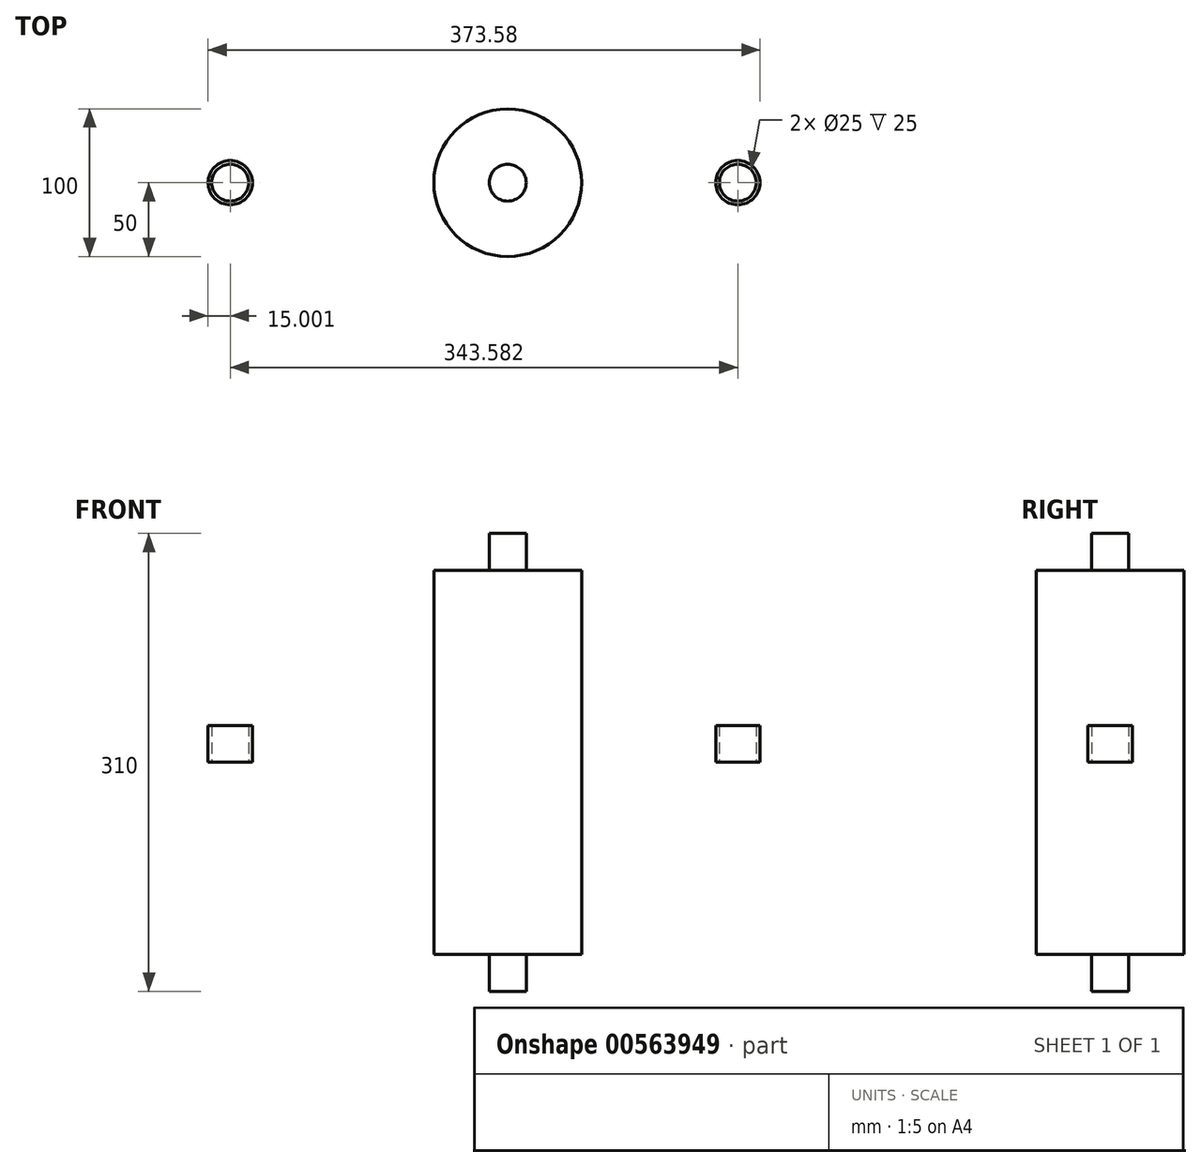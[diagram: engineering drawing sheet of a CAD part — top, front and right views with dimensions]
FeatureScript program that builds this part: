
annotation { "Feature Type Name" : "Feature", "Feature Type Description" : "" }
export const myFeature = defineFeature(function(context is Context, id is Id, definition is map)
    precondition{}
    {
        {
            var Q0;
            Q0=qCreatedBy(makeId("Top.planeOp"),FACE);
            var sketch = newSketch(context, id + "F0", { "sketchPlane" : qUnion([Q0])});
            skCircle(sketch, "E0", {"center": v(0, 0) * mm, "radius": 50 * mm});
            skCircle(sketch, "E1", {"center": v(0, 0) * mm, "radius": 12.5 * mm});
            skSolve(sketch);
        }
        {
            var Q0;
            Q0=makeQuery(id+"F0.imprint","IMPRINT",FACE,{"disambiguationData":[TD([[makeQuery(id+"F0.imprint","IMPRINT",EDGE,{"derivedFrom":sQuery(id+"F0.wireOp",EDGE,"E1")}),1.0]])]});
            extrude(context, id + "F1", {"entities" : qUnion([Q0]), "endBound" : BoundingType.SYMMETRIC, "depth" : 310 * mm, "offsetDistance" : 25 * mm});
        }
        {
            var Q0;
            Q0=qSketchRegion(id+"F0",true);
            extrude(context, id + "F2", {"entities" : qUnion([Q0]), "operationType" : NewBodyOperationType.ADD, "endBound" : BoundingType.SYMMETRIC, "depth" : 260 * mm, "offsetDistance" : 25 * mm});
        }
        {
            var Q0;
            Q0=qCreatedBy(makeId("Top.planeOp"),FACE);
            var sketch = newSketch(context, id + "F3", { "sketchPlane" : qUnion([Q0])});
            skCircle(sketch, "E2", {"center": v(-187.8, 0) * mm, "radius": 15 * mm});
            skCircle(sketch, "E3", {"center": v(-187.8, 0) * mm, "radius": 12.5 * mm});
            skCircle(sketch, "E4", {"center": v(155.78, 0) * mm, "radius": 15 * mm});
            skCircle(sketch, "E5", {"center": v(155.78, 0) * mm, "radius": 12.5 * mm});
            skSolve(sketch);
        }
        {
            var Q0;
            Q0=qSketchRegion(id+"F3",true);
            extrude(context, id + "F4", {"entities" : qUnion([Q0]), "depth" : 25 * mm, "offsetDistance" : 25 * mm});
        }
    });
